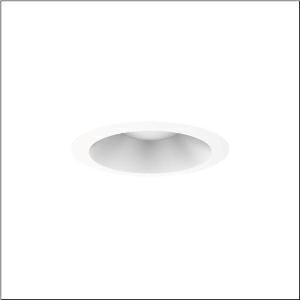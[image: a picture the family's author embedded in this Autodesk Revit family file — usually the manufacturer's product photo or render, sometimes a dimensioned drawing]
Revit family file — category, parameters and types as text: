
# Revit family: lunis_31_midi_51dn15dg42
name_source: partatom
category: Lighting Fixtures
units: mm (PartAtom-declared; Revit-internal decimal feet)

## family parameters
Cut with Voids When Loaded = No
Host = Face
Light Source = No
Part Type = Normal
Room Calculation Point = No
Round Connector Dimension = Use Diameter
Shared = No

## types (1)
- Lunis 31 midi (1 x LED, 2150 lm, 17 W, 4000K)
    Apparent Load = 17 VA
    CIE Flux Codes = 89 99 100 100 100
    Color Rendering = 80
    Color Temperature = 4000K
    Default Elevation = 1800 mm
    Description = Lunis 31,  midi, downlight, light control with lens, light emission: direct distribution, LED rated luminous flux: 2.150lm, light colour: 840, mains connection: 220..240V, AC, 50/60Hz, housing, white, protection rating (complete): IP20, protection rating (on room side): IP54, insulation class (complete): insulation class II (safety insulation), certification: CE, packaging unit: 1 piece
    Height = 0 mm  [stored 0 ft]
    Lamp = 1 x LED
    Lamp Light Flux = 2150 lm
    Lamp Power = 17 W
    Lamp count = 1
    Length = 259 mm
    Luminous efficacy = 126 lm/W
    Manufacturer = Siteco
    ModVariant = No
    Model = 51DN15DG42
    Mounting Place = Ceiling
    Mounting Type = Recessed
    Number of Poles = 1
    OnlyDefault = Yes
    Power Factor = 1
    Product Name = Lunis 31 midi
    Product group = downlight
    ProductGroupID = 400
    Protection Class = Protection class II
    Protection Degree = IP 20
    RLX_Detail_Level = 1
    RLX_Emergency_Light_Flux = 0 lm
    RLX_Emergency_Type = 0
    RLX_Emergency_Type_DB = No
    RlxData = <blob elided: 23605 chars, md5=307f7f55>
    Socket = socket
    Standby Power = 0 W
    System Light Flux = 2150 lm
    System Power = 17 W
    Type Comments = Product without accessories
    Type Image = l_1006711.jpg
    URL = http://relux.com
    VarID = ---
    Voltage = 0 V
    Weight = 0.00 kg
    Width = 0 mm  [stored 0 ft]

note: [stored X ft] marks values corroborated as IEEE doubles in the binary element streams (Revit-internal decimal feet)

## geometry (parser evidence)
native form markers: Blend x4, Sweep x12
no freeform markers — native parametric forms only
